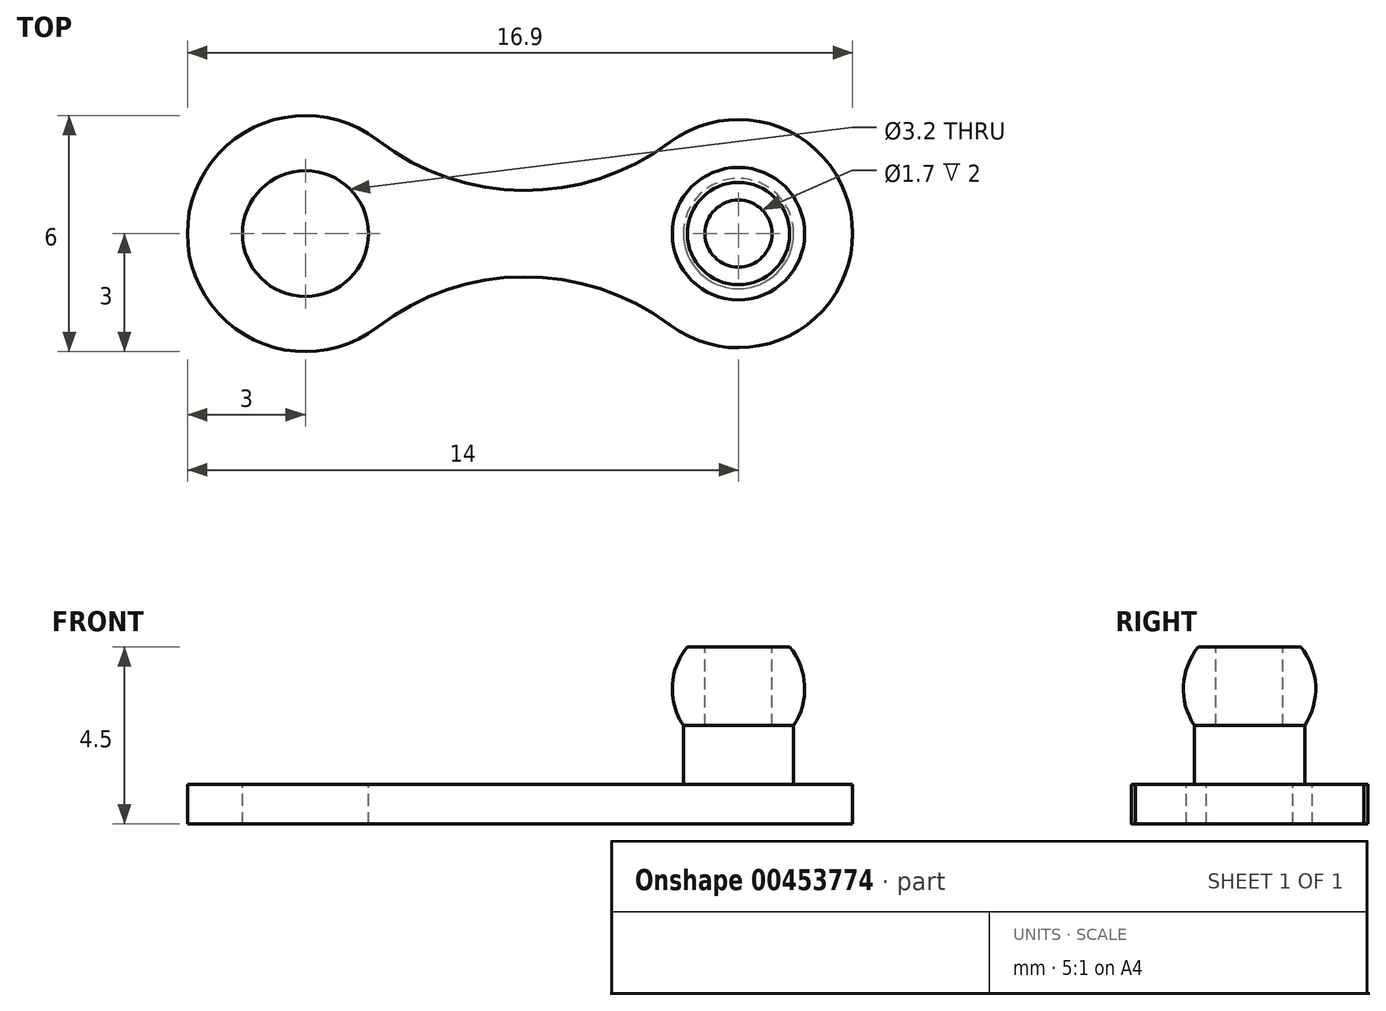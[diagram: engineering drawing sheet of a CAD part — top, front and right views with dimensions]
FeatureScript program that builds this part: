
annotation { "Feature Type Name" : "Feature", "Feature Type Description" : "" }
export const myFeature = defineFeature(function(context is Context, id is Id, definition is map)
    precondition{}
    {
        {
            var Q0;
            Q0=qCreatedBy(makeId("Top.planeOp"),FACE);
            var sketch = newSketch(context, id + "F0", { "sketchPlane" : qUnion([Q0])});
            skCircle(sketch, "E0", {"center": v(0, 0) * mm, "radius": 1.4 * mm});
            skSolve(sketch);
        }
        {
            var Q0;
            Q0=qCreatedBy(makeId("Front.planeOp"),FACE);
            var sketch = newSketch(context, id + "F1", { "sketchPlane" : qUnion([Q0])});
            skLineSegment(sketch, "E1", {"start": v(0, 0) * mm, "end": v(0, 2) * mm});
            skLineSegment(sketch, "E2", {"start": v(0, 2) * mm, "end": v(-1.3, 2) * mm});
            skArc(sketch, "E3", {"start": v(-1.3, 2) * mm, "mid": v(-1.68, 1.02) * mm, "end": v(-1.4, 0) * mm});
            skLineSegment(sketch, "E4", {"start": v(-1.4, 0) * mm, "end": v(0, 0) * mm});
            skSolve(sketch);
        }
        {
            var Q0;
            Q0 = qSketchRegion(id + "F1", true);
            var Q1;
            Q1=sQuery(id+"F1.wireOp",EDGE,"E1");
            revolve(context, id + "F2", {"entities" : qUnion([Q0]), "axis" : qUnion([Q1]), "revolveType" : RevolveType.FULL});
        }
        {
            var Q0;
            Q0=makeQuery(id+"F0.imprint","IMPRINT",FACE,{"disambiguationData":[TD([[makeQuery(id+"F0.imprint","IMPRINT",EDGE,{"derivedFrom":sQuery(id+"F0.wireOp",EDGE,"E0")}),1.0]])]});
            extrude(context, id + "F3", {"entities" : qUnion([Q0]), "operationType" : NewBodyOperationType.ADD, "oppositeDirection" : true, "depth" : 1.5 * mm});
        }
        {
            var Q0;
            Q0=makeQuery(id+"F3.opExtrude","CAP_FACE",FACE,{"disambiguationData":[OSD([sQuery(id+"F0.wireOp",EDGE,"E0")])],"isStart":false});
            var sketch = newSketch(context, id + "F4", { "sketchPlane" : qUnion([Q0])});
            skCircle(sketch, "E5", {"center": v(0, 0) * mm, "radius": 2.9 * mm});
            skCircle(sketch, "E6", {"center": v(-11, 0) * mm, "radius": 1.6 * mm});
            skCircle(sketch, "E7", {"center": v(-11, 0) * mm, "radius": 3 * mm});
            skArc(sketch, "E8", {"start": v(-9.17, 2.38) * mm, "mid": v(-5.46, 1.1) * mm, "end": v(-1.74, 2.32) * mm});
            skLineSegment(sketch, "E9", {"start": v(-11, 0) * mm, "end": v(0, 0) * mm, "construction": true});
            skArc(sketch, "E10.MirrorCS", {"start": v(-9.17, -2.38) * mm, "mid": v(-5.46, -1.1) * mm, "end": v(-1.74, -2.32) * mm});
            skSolve(sketch);
        }
        {
            var Q0;
            {var subQ0=sQuery(id+"F4.wireOp",EDGE,"E8");Q0=makeQuery(id+"F4.imprint","IMPRINT",FACE,{"disambiguationData":[TD([[makeQuery(id+"F4.imprint","IMPRINT",EDGE,{"derivedFrom":subQ0}),-1.0]])]});}
            var Q1;
            Q1=makeQuery(id+"F4.imprint","IMPRINT",FACE,{"disambiguationData":[TD([[makeQuery(id+"F4.imprint","IMPRINT",EDGE,{"derivedFrom":makeQuery(id+"F3.opExtrude","CAP_EDGE",EDGE,{"disambiguationData":[OSD([sQuery(id+"F0.wireOp",EDGE,"E0")])],"isStart":false})}),1.0]])]});
            var Q2;
            Q2=makeQuery(id+"F4.imprint","IMPRINT",FACE,{"disambiguationData":[TD([[makeQuery(id+"F4.imprint","IMPRINT",EDGE,{"derivedFrom":sQuery(id+"F4.wireOp",EDGE,"E6")}),-1.0]])]});
            var Q3;
            Q3=makeQuery(id+"F4.imprint","IMPRINT",FACE,{"disambiguationData":[TD([[makeQuery(id+"F4.imprint","IMPRINT",EDGE,{"derivedFrom":makeQuery(id+"F3.opExtrude","CAP_EDGE",EDGE,{"disambiguationData":[OSD([sQuery(id+"F0.wireOp",EDGE,"E0")])],"isStart":false})}),-1.0]])]});
            extrude(context, id + "F5", {"entities" : qUnion([Q0, Q1, Q2, Q3]), "operationType" : NewBodyOperationType.ADD, "depth" : 1 * mm});
        }
        {
            var Q0;
            Q0=makeQuery(id+"F2.opRevolve","SWEPT_FACE",FACE,{"disambiguationData":[OSD([sQuery(id+"F1.wireOp",EDGE,"E2")])]});
            var sketch = newSketch(context, id + "F6", { "sketchPlane" : qUnion([Q0])});
            skCircle(sketch, "E11", {"center": v(0, 0) * mm, "radius": 0.85 * mm});
            skSolve(sketch);
        }
        {
            var Q0;
            Q0 = qSketchRegion(id + "F6", true);
            extrude(context, id + "F7", {"entities" : qUnion([Q0]), "operationType" : NewBodyOperationType.REMOVE, "oppositeDirection" : true, "depth" : 2 * mm});
        }
    });
